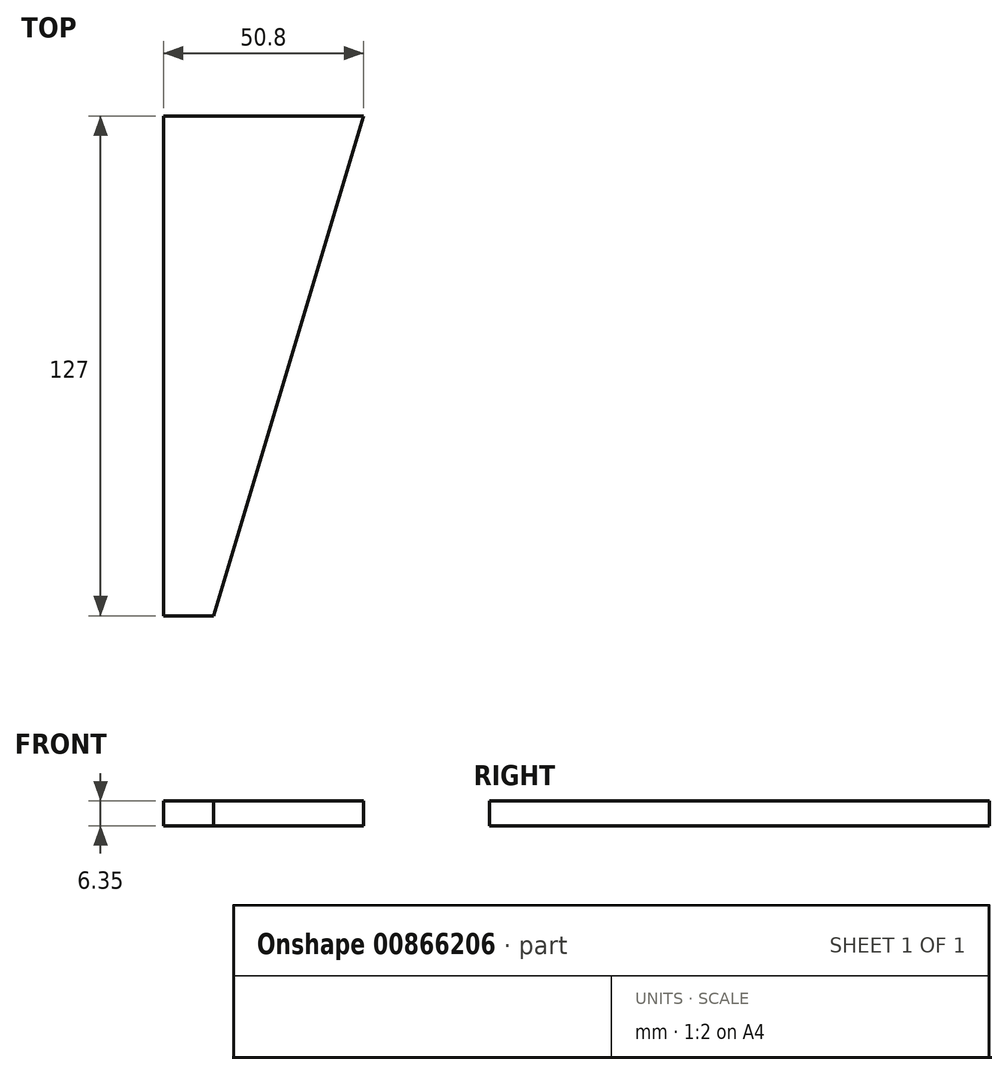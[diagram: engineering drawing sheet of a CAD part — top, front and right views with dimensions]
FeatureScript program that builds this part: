
annotation { "Feature Type Name" : "Feature", "Feature Type Description" : "" }
export const myFeature = defineFeature(function(context is Context, id is Id, definition is map)
    precondition{}
    {
        {
            var Q0;
            Q0=qCreatedBy(makeId("Top.planeOp"),FACE);
            var sketch = newSketch(context, id + "F0", { "sketchPlane" : qUnion([Q0])});
            skLineSegment(sketch, "E0", {"start": v(0, 0) * mm, "end": v(-50.8, 0) * mm});
            skLineSegment(sketch, "E1", {"start": v(-50.8, 0) * mm, "end": v(-50.8, -127) * mm});
            skLineSegment(sketch, "E2", {"start": v(-50.8, -127) * mm, "end": v(-38.1, -127) * mm});
            skLineSegment(sketch, "E3", {"start": v(0, 0) * mm, "end": v(-38.1, -127) * mm});
            skSolve(sketch);
        }
        {
            var Q0;
            Q0=makeQuery(id+"F0.imprint","IMPRINT",FACE,{"disambiguationData":[TD([[makeQuery(id+"F0.imprint","IMPRINT",EDGE,{"derivedFrom":sQuery(id+"F0.wireOp",EDGE,"E0")}),1.0]])]});
            extrude(context, id + "F1", {"entities" : qUnion([Q0]), "depth" : 6.35 * mm, "offsetDistance" : 25.4 * mm});
        }
    });
